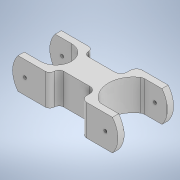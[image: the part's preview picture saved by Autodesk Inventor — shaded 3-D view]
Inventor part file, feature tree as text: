
AUTODESK INVENTOR PART (.ipt)
format: ipt  version: 2022 (Build 260153000, 153)  size: 203,776 bytes
history: native  units: mm
features: fillet x6, extrude x4, sketch x4
ambient origin geometry x8: Origin, YZ Plane, XZ Plane, XY Plane, X Axis, Y Axis, Z Axis, Center Point
bodies: Solid1 (feature_tree)
feature tree (14):
  extrude  "Extrusion1"  Depth=50.0mm TaperAngle=0.0deg
  extrude  "Extrusion2"  Depth=10.0mm
  fillet  "Fillet1"  Radius=20.0mm
  fillet  "Fillet2"  Radius=10.0mm
  fillet  "Fillet3"  Radius=10.0mm
  fillet  "Fillet4"  Radius=10.0mm
  fillet  "Fillet5"  Radius=10.0mm
  fillet  "Fillet6"  Radius=20.0mm
  extrude  "Extrusion3"  Depth=10.0mm
  extrude  "Extrusion4"  Depth=10.0mm
  sketch  "Sketch1"  dims[d0=100.0mm d3=50.0mm d4=0.0mm]
  sketch  "Sketch2"  dims[d5=60.0mm d13=20.0mm d14=20.0mm d18=10.0mm d19=10.0mm d25=10.0mm d26=10.0mm d27=20.0mm]
  sketch  "Sketch3"  dims[d28=10.0mm d29=10.0mm]
  sketch  "Sketch4"  dims[d31=50.0mm d32=0.0mm d33=10.0mm d34=10.0mm d35=10.0mm d36=10.0mm d37=7.5mm d38=7.5mm d41=200.0mm d42=0.0mm d44=5.0mm d46=5.0mm d47=200.0mm d48=0.0mm]
